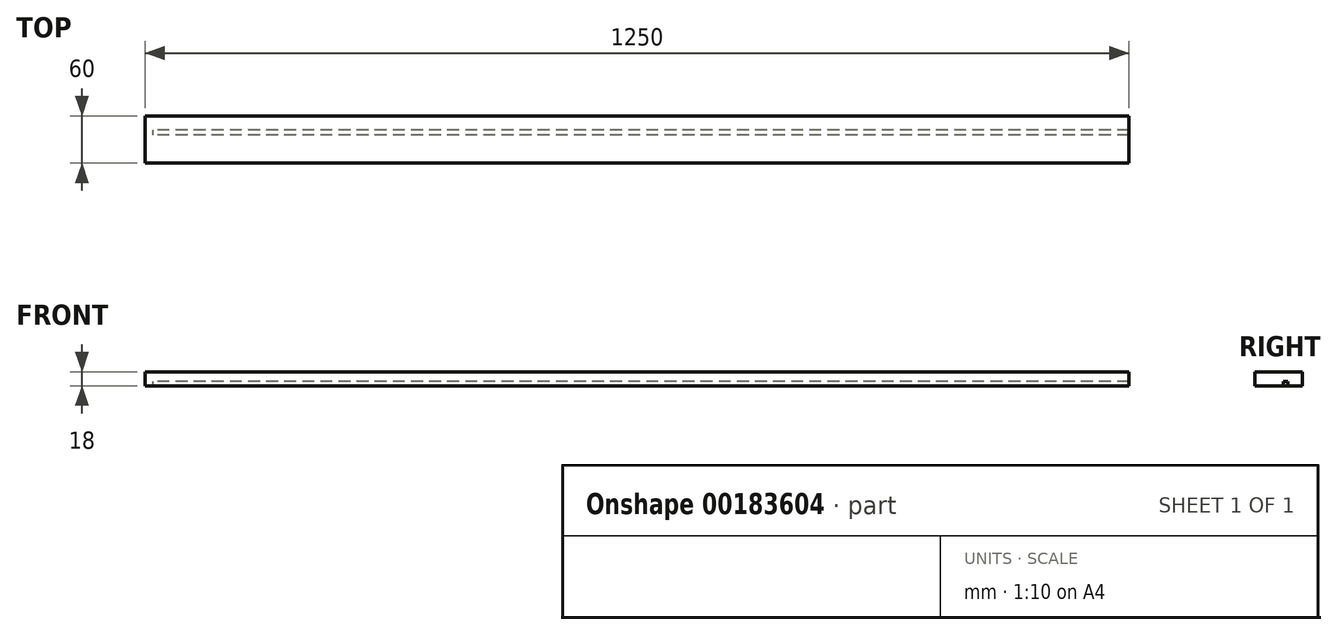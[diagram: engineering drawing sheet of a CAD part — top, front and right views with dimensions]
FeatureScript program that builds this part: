
annotation { "Feature Type Name" : "Feature", "Feature Type Description" : "" }
export const myFeature = defineFeature(function(context is Context, id is Id, definition is map)
    precondition{}
    {
        {
            var Q0;
            Q0=qCreatedBy(makeId("Top.planeOp"),FACE);
            var sketch = newSketch(context, id + "F0", { "sketchPlane" : qUnion([Q0])});
            skLineSegment(sketch, "E0.bottom", {"start": v(625, -30) * mm, "end": v(-625, -30) * mm});
            skLineSegment(sketch, "E0.top", {"start": v(625, 30) * mm, "end": v(-625, 30) * mm});
            skLineSegment(sketch, "E0.left", {"start": v(625, -30) * mm, "end": v(625, 30) * mm});
            skLineSegment(sketch, "E0.right", {"start": v(-625, -30) * mm, "end": v(-625, 30) * mm});
            skPoint(sketch, "E0.middle", {"position": v(0, 0) * mm});
            skSolve(sketch);
        }
        {
            var Q0;
            Q0 = qSketchRegion(id + "F0", true);
            extrude(context, id + "F1", {"entities" : qUnion([Q0]), "depth" : 18 * mm});
        }
        {
            var Q0;
            Q0=makeQuery(id+"F1.opExtrude","CAP_FACE",FACE,{"disambiguationData":[OSD([sQuery(id+"F0.wireOp",EDGE,"E0.bottom"),sQuery(id+"F0.wireOp",EDGE,"E0.top"),sQuery(id+"F0.wireOp",EDGE,"E0.left"),sQuery(id+"F0.wireOp",EDGE,"E0.right")])],"isStart":true});
            var sketch = newSketch(context, id + "F2", { "sketchPlane" : qUnion([Q0])});
            skLineSegment(sketch, "E1.bottom", {"start": v(625, -12) * mm, "end": v(-615, -12) * mm});
            skLineSegment(sketch, "E1.top", {"start": v(625, -6) * mm, "end": v(-615, -6) * mm});
            skLineSegment(sketch, "E1.left", {"start": v(625, -12) * mm, "end": v(625, -6) * mm});
            skLineSegment(sketch, "E1.right", {"start": v(-615, -12) * mm, "end": v(-615, -6) * mm});
            skPoint(sketch, "E1.middle", {"position": v(5, -9) * mm});
            skSolve(sketch);
        }
        {
            var Q0;
            Q0 = qSketchRegion(id + "F2", true);
            extrude(context, id + "F3", {"entities" : qUnion([Q0]), "operationType" : NewBodyOperationType.REMOVE, "oppositeDirection" : true, "depth" : 6 * mm});
        }
    });
